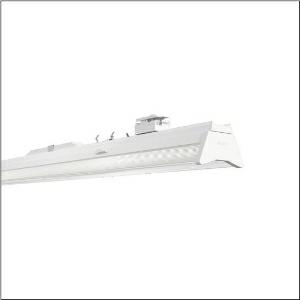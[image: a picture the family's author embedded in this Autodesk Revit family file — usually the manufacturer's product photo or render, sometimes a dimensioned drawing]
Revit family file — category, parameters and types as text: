
# Revit family: licross_21_performance_ho_52td16cn4c5m
name_source: partatom
category: Lighting Fixtures
units: mm (PartAtom-declared; Revit-internal decimal feet)

## family parameters
Cut with Voids When Loaded = No
Host = Face
Light Source = No
Part Type = Normal
Room Calculation Point = No
Round Connector Dimension = Use Diameter
Shared = No

## types (1)
- --- (1 x LED, 12610 lm, 68.9 W, 4000K)
    Apparent Load = 69 VA
    CIE Flux Codes = 63 87 95 78 100
    Color Rendering = 80
    Color Temperature = 4000K
    Default Elevation = 1800 mm
    Description = Licross 21 Performance HO, luminaire insert, of sheet steel, galvanised, coil coated, white, length: 1.500mm, width: 120mm, height: 123mm, LED rated luminous flux: 12.610lm, light colour: 840, SDCM (Standard Deviation of Colour Matching)MacAdam ≤ 3 SDCM (initial), control gear: ON/OFF Multilumen, CLOi, with plug, 3-pole, with phase selection, mains connection: 220..240V, AC, 50/60Hz, start of lifetime: 69W, end of service life: 83W, internal wiring halogen-free, primary light control with lens, of plastic, primary optical cover: cover, of PMMA, light emission: direct/indirect distribution, primary light characteristic: symmetric, protection rating (complete): IP54, insulation class (complete): insulation class I (protective earthing), certification: CE, ENEC, UKCA, protection symbol: D if used in an environment with non-conductive dust loads with corresponding accessories, impact resistance: IK06, permissible ambient temperature for indoor applications: -35..+35°C, corresponds to IFS (International Featured Standards) requirements for safety and quality in the food industry, reducing of maximum allowable ambient temperature of 5°C with ceiling mounting, LABS conformity tested according to VDMA 24364:2018-05, The light source and the operating device comply with the requirements of the Ecodesign Regulation (EU) 2019/2020 and are replaceable in accordance with this regulation, packaging unit: 1 piece
    Height = 114 mm
    Lamp = 1 x LED
    Lamp Light Flux = 12610 lm
    Lamp Power = 68.9 W
    Lamp count = 1
    Length = 1500 mm
    Luminous efficacy = 183 lm/W
    Manufacturer = Siteco
    ModVariant = No
    Model = 52TD16CN4C5M
    Mounting Place = Ceiling
    Mounting Type = Pendant
    Number of Poles = 1
    OnlyDefault = Yes
    Power Factor = 1
    Product Name = Licross 21 Performance HO
    Product group = luminaire insert | ceiling pendant
    ProductGroupID = 901
    Protection Class = Protection class I
    Protection Degree = IP 54
    RLX_Detail_Level = 1
    RLX_Emergency_Light_Flux = 0 lm
    RLX_Emergency_Type = 0
    RLX_Emergency_Type_DB = No
    RlxData = <blob elided: 32073 chars, md5=d26cf0cf>
    Socket = socket
    Standby Power = 0 W
    System Light Flux = 12610 lm
    System Power = 69 W
    Type Comments = factory setting: luminous flux: 100 % | (A | C | E) | 162 mA
    Type Image = l_1256138.jpg
    URL = http://relux.com
    VarID = @adj_111561
    Voltage = 0 V
    Weight = 0.00 kg
    Width = 120 mm

## geometry (parser evidence)
native form markers: Blend x4, Sweep x13
no freeform markers — native parametric forms only
